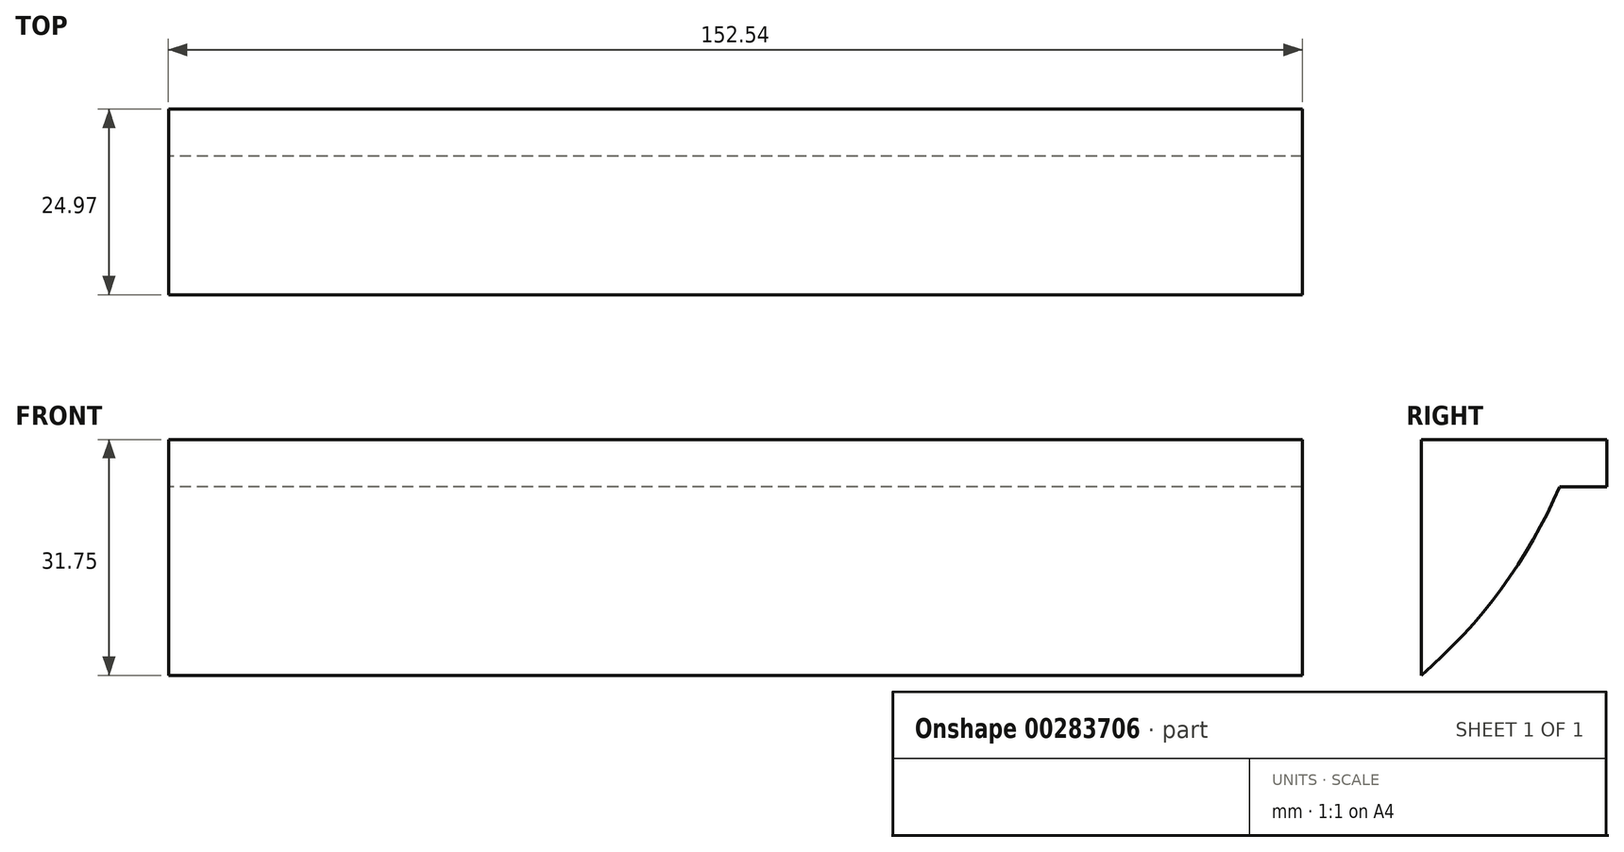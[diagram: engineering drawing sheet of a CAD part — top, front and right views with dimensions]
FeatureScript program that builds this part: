
annotation { "Feature Type Name" : "Feature", "Feature Type Description" : "" }
export const myFeature = defineFeature(function(context is Context, id is Id, definition is map)
    precondition{}
    {
        {
            var Q0;
            Q0=qCreatedBy(makeId("Top.planeOp"),FACE);
            var sketch = newSketch(context, id + "F0", { "sketchPlane" : qUnion([Q0])});
            skLineSegment(sketch, "E0.bottom", {"start": v(-76.27, 0) * mm, "end": v(76.27, 0) * mm});
            skLineSegment(sketch, "E0.top", {"start": v(-76.27, 24.18) * mm, "end": v(76.27, 24.18) * mm});
            skLineSegment(sketch, "E0.left", {"start": v(-76.27, 0) * mm, "end": v(-76.27, 24.18) * mm});
            skLineSegment(sketch, "E0.right", {"start": v(76.27, 0) * mm, "end": v(76.27, 24.18) * mm});
            skSolve(sketch);
        }
        {
            var Q0;
            Q0=makeQuery(id+"F0.imprint","IMPRINT",FACE,{"disambiguationData":[TD([[makeQuery(id+"F0.imprint","IMPRINT",EDGE,{"derivedFrom":sQuery(id+"F0.wireOp",EDGE,"E0.bottom")}),1.0]])]});
            extrude(context, id + "F1", {"entities" : qUnion([Q0]), "depth" : 25.4 * mm});
        }
        {
            var Q0;
            Q0=makeQuery(id+"F1.opExtrude","CAP_EDGE",EDGE,{"disambiguationData":[OSD([sQuery(id+"F0.wireOp",EDGE,"E0.top")])],"isStart":true});
            fillet(context, id + "F2", {"entities" : qUnion([Q0]), "radius" : 69.3 * mm, "tangentPropagation" : true, "allowEdgeOverflow" : false});
        }
        {
            var Q0;
            Q0=makeQuery(id+"F1.opExtrude","CAP_FACE",FACE,{"disambiguationData":[OSD([sQuery(id+"F0.wireOp",EDGE,"E0.bottom"),sQuery(id+"F0.wireOp",EDGE,"E0.top"),sQuery(id+"F0.wireOp",EDGE,"E0.left"),sQuery(id+"F0.wireOp",EDGE,"E0.right")])],"isStart":false});
            extrude(context, id + "F3", {"entities" : qUnion([Q0]), "operationType" : NewBodyOperationType.ADD, "depth" : 6.35 * mm});
        }
        {
            var Q0;
            Q0=makeQuery(id+"F3.opExtrude","SWEPT_FACE",FACE,{"disambiguationData":[OSD([sQuery(id+"F0.wireOp",EDGE,"E0.bottom"),sQuery(id+"F0.wireOp",EDGE,"E0.top"),sQuery(id+"F0.wireOp",EDGE,"E0.left"),sQuery(id+"F0.wireOp",EDGE,"E0.right")])]});
            extrude(context, id + "F4", {"entities" : qUnion([Q0]), "operationType" : NewBodyOperationType.ADD, "depth" : 6.35 * mm});
        }
    });
